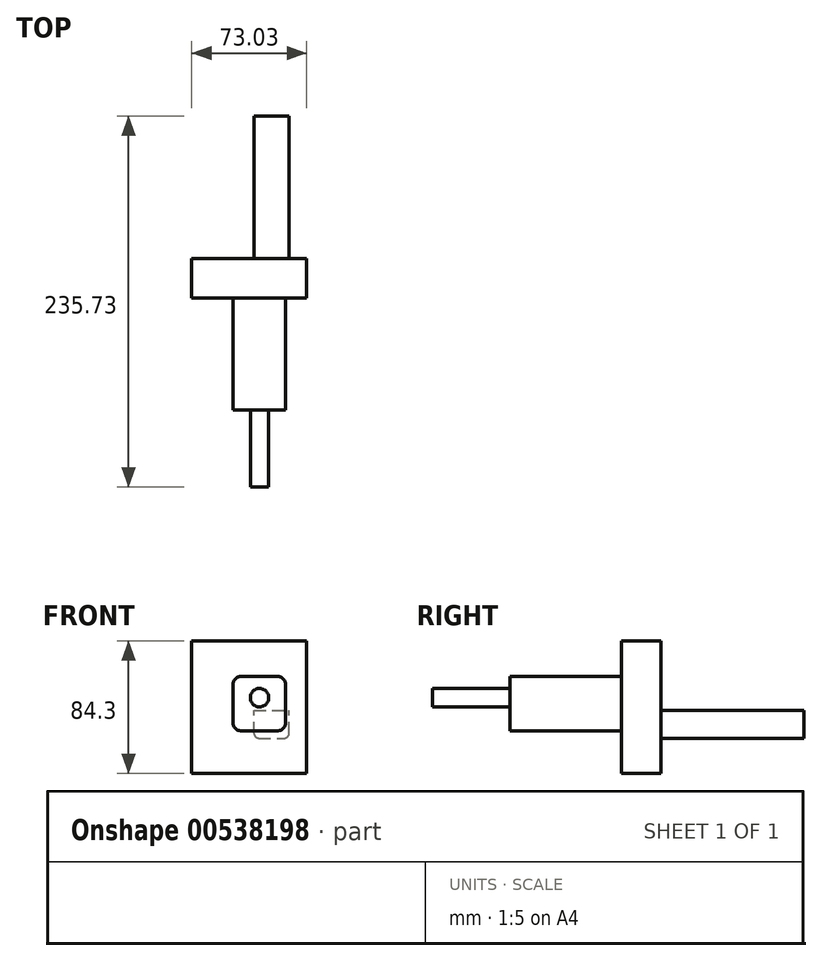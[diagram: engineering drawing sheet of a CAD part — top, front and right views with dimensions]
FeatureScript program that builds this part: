
annotation { "Feature Type Name" : "Feature", "Feature Type Description" : "" }
export const myFeature = defineFeature(function(context is Context, id is Id, definition is map)
    precondition{}
    {
        {
            var Q0;
            Q0=qCreatedBy(makeId("Front.planeOp"),FACE);
            var sketch = newSketch(context, id + "F0", { "sketchPlane" : qUnion([Q0])});
            skLineSegment(sketch, "E0.bottom", {"start": v(-13.48, 44.2) * mm, "end": v(59.55, 44.2) * mm});
            skLineSegment(sketch, "E0.top", {"start": v(-13.48, -40.11) * mm, "end": v(59.55, -40.11) * mm});
            skLineSegment(sketch, "E0.left", {"start": v(-13.48, 44.2) * mm, "end": v(-13.48, -40.11) * mm});
            skLineSegment(sketch, "E0.right", {"start": v(59.55, 44.2) * mm, "end": v(59.55, -40.11) * mm});
            skSolve(sketch);
        }
        {
            var Q0;
            Q0 = qSketchRegion(id + "F0", true);
            extrude(context, id + "F1", {"entities" : qUnion([Q0]), "depth" : 25 * mm, "offsetDistance" : 25 * mm});
        }
        {
            var Q0;
            Q0=makeQuery(id+"F1.opExtrude","CAP_FACE",FACE,{"disambiguationData":[OSD([sQuery(id+"F0.wireOp",EDGE,"E0.bottom"),sQuery(id+"F0.wireOp",EDGE,"E0.top"),sQuery(id+"F0.wireOp",EDGE,"E0.left"),sQuery(id+"F0.wireOp",EDGE,"E0.right")])],"isStart":false});
            var sketch = newSketch(context, id + "F2", { "sketchPlane" : qUnion([Q0])});
            skLineSegment(sketch, "E1.bottom", {"start": v(12.82, -13.04) * mm, "end": v(46.1, -13.04) * mm});
            skLineSegment(sketch, "E1.top", {"start": v(12.82, 21.51) * mm, "end": v(46.1, 21.51) * mm});
            skLineSegment(sketch, "E1.left", {"start": v(12.82, -13.04) * mm, "end": v(12.82, 21.51) * mm});
            skLineSegment(sketch, "E1.right", {"start": v(46.1, -13.04) * mm, "end": v(46.1, 21.51) * mm});
            skSolve(sketch);
        }
        {
            var Q0;
            Q0 = qSketchRegion(id + "F2", true);
            extrude(context, id + "F3", {"entities" : qUnion([Q0]), "operationType" : NewBodyOperationType.ADD, "depth" : 71 * mm, "offsetDistance" : 25 * mm});
        }
        {
            var Q0;
            Q0=makeQuery(id+"F3.opExtrude","SWEPT_EDGE",EDGE,{"disambiguationData":[OSD([sQuery(id+"F2.wireOp",EDGE,"E1.bottom"),sQuery(id+"F2.wireOp",EDGE,"E1.right")])]});
            var Q1;
            Q1=makeQuery(id+"F3.opExtrude","SWEPT_EDGE",EDGE,{"disambiguationData":[OSD([sQuery(id+"F2.wireOp",EDGE,"E1.top"),sQuery(id+"F2.wireOp",EDGE,"E1.right")])]});
            var Q2;
            Q2=makeQuery(id+"F3.opExtrude","SWEPT_EDGE",EDGE,{"disambiguationData":[OSD([sQuery(id+"F2.wireOp",EDGE,"E1.top"),sQuery(id+"F2.wireOp",EDGE,"E1.left")])]});
            var Q3;
            Q3=makeQuery(id+"F3.opExtrude","SWEPT_EDGE",EDGE,{"disambiguationData":[OSD([sQuery(id+"F2.wireOp",EDGE,"E1.bottom"),sQuery(id+"F2.wireOp",EDGE,"E1.left")])]});
            fillet(context, id + "F4", {"entities" : qUnion([Q0, Q1, Q2, Q3]), "radius" : 5 * mm, "tangentPropagation" : true, "allowEdgeOverflow" : false});
        }
        {
            var Q0;
            Q0=makeQuery(id+"F3.opExtrude","CAP_FACE",FACE,{"disambiguationData":[OSD([sQuery(id+"F2.wireOp",EDGE,"E1.bottom"),sQuery(id+"F2.wireOp",EDGE,"E1.top"),sQuery(id+"F2.wireOp",EDGE,"E1.left"),sQuery(id+"F2.wireOp",EDGE,"E1.right")])],"isStart":false});
            var sketch = newSketch(context, id + "F5", { "sketchPlane" : qUnion([Q0])});
            skCircle(sketch, "E2", {"center": v(29.61, 8) * mm, "radius": 5.84 * mm});
            skSolve(sketch);
        }
        {
            var Q0;
            Q0 = qSketchRegion(id + "F5", true);
            extrude(context, id + "F6", {"entities" : qUnion([Q0]), "operationType" : NewBodyOperationType.ADD, "depth" : 49.1 * mm, "offsetDistance" : 25 * mm});
        }
        {
            var Q0;
            Q0=makeQuery(id+"F1.opExtrude","CAP_FACE",FACE,{"disambiguationData":[OSD([sQuery(id+"F0.wireOp",EDGE,"E0.bottom"),sQuery(id+"F0.wireOp",EDGE,"E0.top"),sQuery(id+"F0.wireOp",EDGE,"E0.left"),sQuery(id+"F0.wireOp",EDGE,"E0.right")])],"isStart":true});
            var sketch = newSketch(context, id + "F7", { "sketchPlane" : qUnion([Q0])});
            skLineSegment(sketch, "E3.bottom", {"start": v(-26.2, -17.73) * mm, "end": v(-48.38, -17.73) * mm});
            skLineSegment(sketch, "E3.top", {"start": v(-26.2, 0) * mm, "end": v(-48.38, 0) * mm});
            skLineSegment(sketch, "E3.left", {"start": v(-26.2, -17.73) * mm, "end": v(-26.2, 0) * mm});
            skLineSegment(sketch, "E3.right", {"start": v(-48.38, -17.73) * mm, "end": v(-48.38, 0) * mm});
            skSolve(sketch);
        }
        {
            var Q0;
            Q0 = qSketchRegion(id + "F7", true);
            extrude(context, id + "F8", {"entities" : qUnion([Q0]), "operationType" : NewBodyOperationType.ADD, "depth" : 90.63 * mm, "offsetDistance" : 25 * mm});
        }
        {
            var Q0;
            Q0=makeQuery(id+"F8.opExtrude","SWEPT_EDGE",EDGE,{"disambiguationData":[OSD([sQuery(id+"F7.wireOp",EDGE,"E3.bottom"),sQuery(id+"F7.wireOp",EDGE,"E3.left")])]});
            var Q1;
            Q1=makeQuery(id+"F8.opExtrude","SWEPT_EDGE",EDGE,{"disambiguationData":[OSD([sQuery(id+"F7.wireOp",EDGE,"E3.bottom"),sQuery(id+"F7.wireOp",EDGE,"E3.right")])]});
            fillet(context, id + "F9", {"entities" : qUnion([Q0, Q1]), "radius" : 3 * mm, "tangentPropagation" : true, "allowEdgeOverflow" : false});
        }
    });
